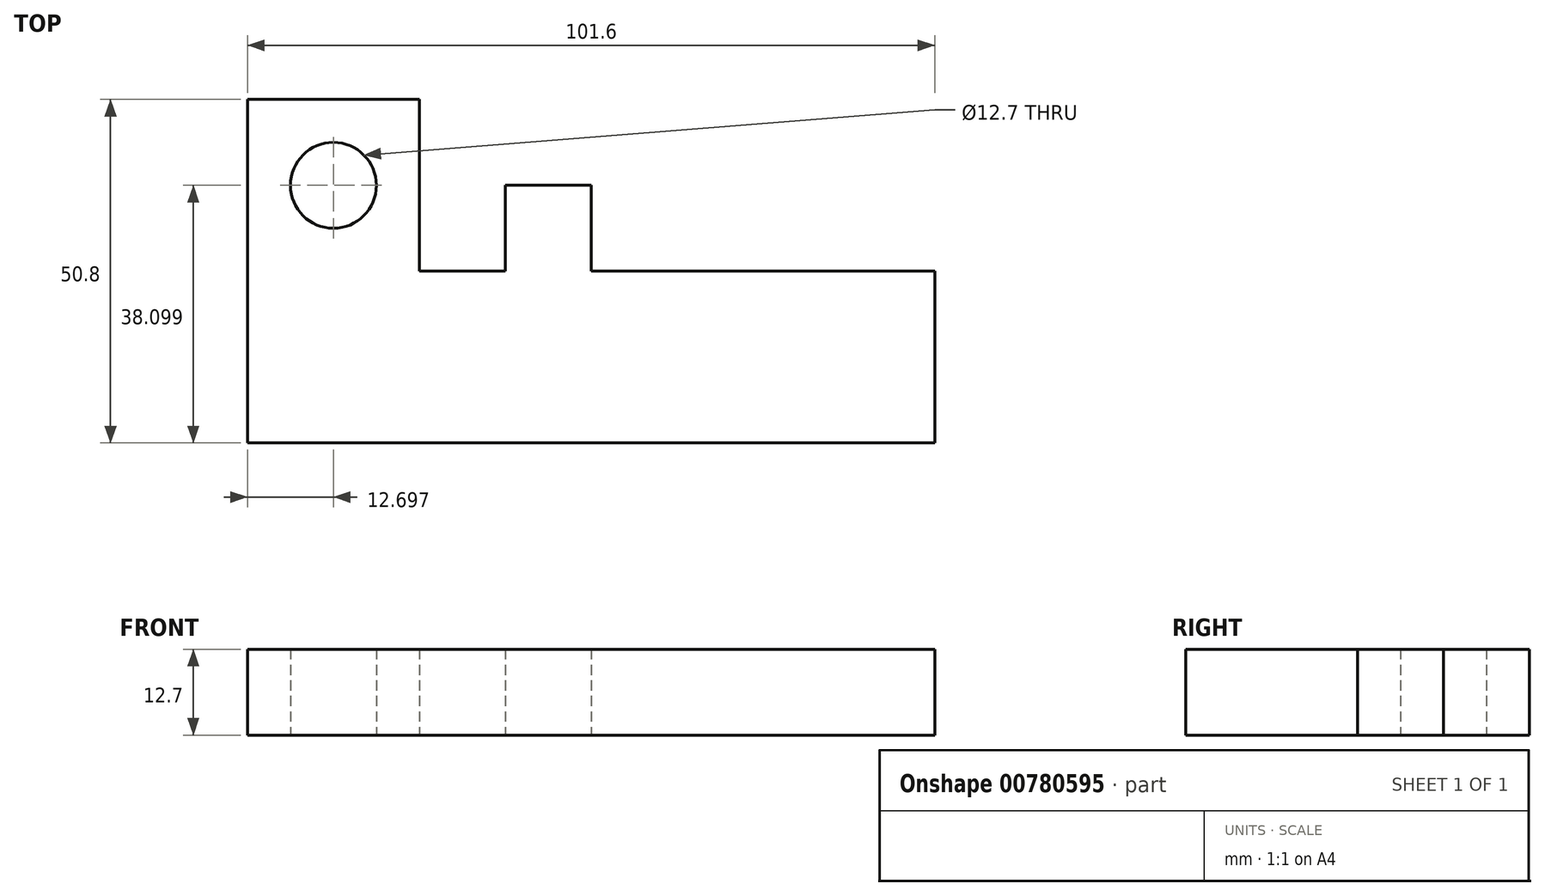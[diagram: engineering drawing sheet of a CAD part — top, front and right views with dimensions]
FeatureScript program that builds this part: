
annotation { "Feature Type Name" : "Feature", "Feature Type Description" : "" }
export const myFeature = defineFeature(function(context is Context, id is Id, definition is map)
    precondition{}
    {
        {
            var Q0;
            Q0=qCreatedBy(makeId("Top.planeOp"),FACE);
            var sketch = newSketch(context, id + "F0", { "sketchPlane" : qUnion([Q0])});
            skLineSegment(sketch, "E0", {"start": v(-36.47, 20.2) * mm, "end": v(-36.47, -30.6) * mm});
            skLineSegment(sketch, "E1", {"start": v(-36.47, -30.6) * mm, "end": v(65.13, -30.6) * mm});
            skLineSegment(sketch, "E2", {"start": v(65.13, -30.6) * mm, "end": v(65.13, -5.2) * mm});
            skLineSegment(sketch, "E3", {"start": v(65.13, -5.2) * mm, "end": v(14.33, -5.2) * mm});
            skLineSegment(sketch, "E4", {"start": v(14.33, -5.2) * mm, "end": v(14.33, 7.5) * mm});
            skLineSegment(sketch, "E5", {"start": v(14.33, 7.5) * mm, "end": v(1.63, 7.5) * mm});
            skLineSegment(sketch, "E6", {"start": v(1.63, 7.5) * mm, "end": v(1.63, -5.2) * mm});
            skLineSegment(sketch, "E7", {"start": v(1.63, -5.2) * mm, "end": v(-11.07, -5.2) * mm});
            skLineSegment(sketch, "E8", {"start": v(-11.07, -5.2) * mm, "end": v(-11.07, 20.2) * mm});
            skLineSegment(sketch, "E9", {"start": v(-11.07, 20.2) * mm, "end": v(-36.47, 20.2) * mm});
            skLineSegment(sketch, "E10", {"start": v(-23.77, 20.2) * mm, "end": v(-23.77, -30.6) * mm, "construction": true});
            skLineSegment(sketch, "E11", {"start": v(-11.07, 7.5) * mm, "end": v(-36.47, 7.5) * mm, "construction": true});
            skCircle(sketch, "E12", {"center": v(-23.77, 7.5) * mm, "radius": 6.35 * mm});
            skSolve(sketch);
        }
        {
            var Q0;
            Q0=qSketchRegion(id+"F0",true);
            extrude(context, id + "F1", {"entities" : qUnion([Q0]), "depth" : 12.7 * mm, "offsetDistance" : 25.4 * mm});
        }
    });
